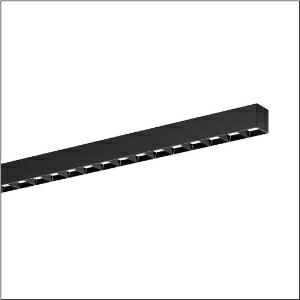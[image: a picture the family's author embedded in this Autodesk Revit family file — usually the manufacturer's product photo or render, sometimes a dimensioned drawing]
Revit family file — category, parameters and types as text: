
# Revit family: silica_r__21_51mx21dc4abb_1522
name_source: partatom
category: Lighting Fixtures
units: mm (PartAtom-declared; Revit-internal decimal feet)

## family parameters
Cut with Voids When Loaded = No
Host = Face
Light Source = No
Part Type = Normal
Room Calculation Point = No
Round Connector Dimension = Use Diameter
Shared = No

## types (1)
- --- (1 x LED, 10800 lm, 64.8 W, 4000K)
    Apparent Load = 65 VA
    CIE Flux Codes = 87 99 100 100 100
    Color Rendering = 80
    Color Temperature = 4000K
    Default Elevation = 1800 mm
    Description = Silica® 21, office luminaire, primary light control with darklight reflector, of PMMA, black, CAT 2 (L<= 3000cd/m²), light emission: direct distribution, primary light characteristic: symmetric, installation type: surface-mounted, LED, rated luminous flux: 10.800lm, luminous efficacy: 167lm/W, light colour: 840, colour temperature: 4000K, with terminal, 3+2-pole, max. 2.5mm², mains connection: 220..240V, AC, 50/60Hz, rated input power: 64.8W, luminaire housing, of aluminium, jet black (RAL 9005), length: 3.004mm, width: 53mm, height: 53mm, protection rating (complete): IP20, insulation class (complete): insulation class I (protective earthing), certification: CE, permissible operating ambient temperature: 0..+35°C, standard: EN 50419, packaging unit: 1 piece
    Height = 0 mm  [stored 0 ft]
    Lamp = 1 x LED
    Lamp Light Flux = 10800 lm
    Lamp Power = 64.8 W
    Lamp count = 1
    Length = 3004 mm
    Luminous efficacy = 167 lm/W
    Manufacturer = Siteco
    ModVariant = No
    Model = 51MX21DC4ABB
    Mounting Place = Ceiling
    Mounting Type = Recessed
    Number of Poles = 1
    OnlyDefault = Yes
    Power Factor = 1
    Product Name = Silica® 21
    Product group = office luminaire | ceiling recessed
    ProductGroupID = 401
    Protection Class = Protection class I
    Protection Degree = IP 20
    RLX_Detail_Level = 1
    RLX_Emergency_Light_Flux = 0 lm
    RLX_Emergency_Type = 0
    RLX_Emergency_Type_DB = No
    RlxData = <blob elided: 64617 chars, md5=92c81eae>
    Socket = socket
    Standby Power = 0 W
    System Light Flux = 10800 lm
    System Power = 65 W
    Type Comments = factory setting: luminous flux: 100 % | dim-lin: 254 | 367 mA
    Type Image = l_1313577.jpg
    URL = http://relux.com
    VarID = @adj_072727
    Voltage = 0 V
    Weight = 0.00 kg
    Width = 53 mm

note: [stored X ft] marks values corroborated as IEEE doubles in the binary element streams (Revit-internal decimal feet)

## geometry (parser evidence)
native form markers: Blend x4, Sweep x11
no freeform markers — native parametric forms only
